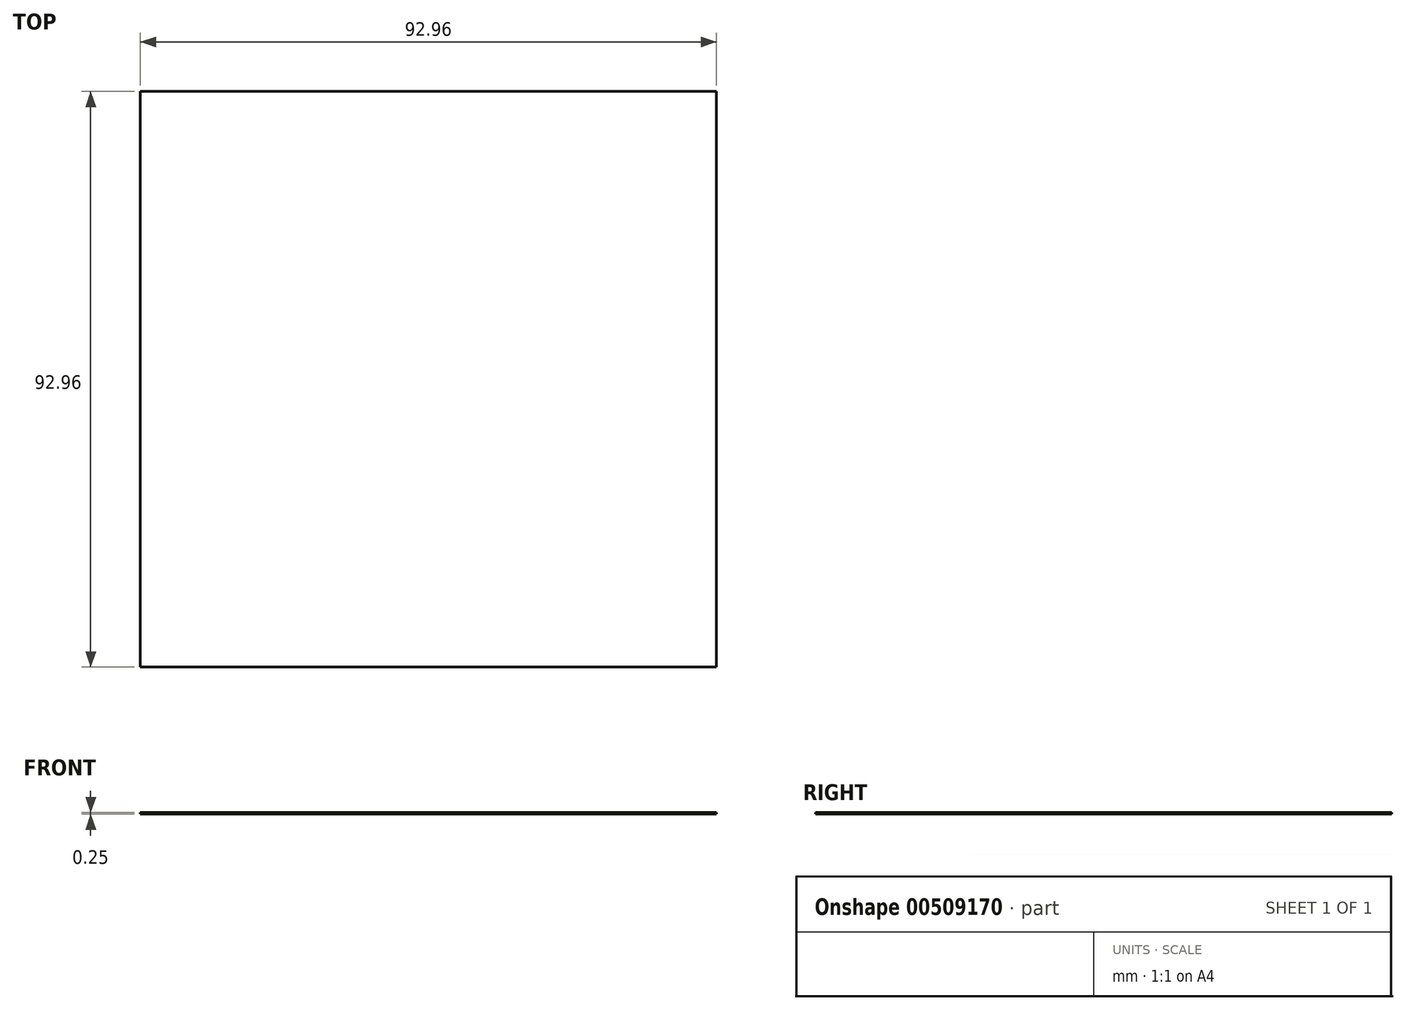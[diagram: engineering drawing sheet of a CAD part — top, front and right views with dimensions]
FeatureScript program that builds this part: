
annotation { "Feature Type Name" : "Feature", "Feature Type Description" : "" }
export const myFeature = defineFeature(function(context is Context, id is Id, definition is map)
    precondition{}
    {
        {
            var Q0;
            Q0=qCreatedBy(makeId("Top.planeOp"),FACE);
            var sketch = newSketch(context, id + "F0", { "sketchPlane" : qUnion([Q0])});
            skLineSegment(sketch, "E0.bottom", {"start": v(-45.47, 44.32) * mm, "end": v(47.49, 44.32) * mm});
            skLineSegment(sketch, "E0.top", {"start": v(-45.47, -48.64) * mm, "end": v(47.49, -48.64) * mm});
            skLineSegment(sketch, "E0.left", {"start": v(-45.47, 44.32) * mm, "end": v(-45.47, -48.64) * mm});
            skLineSegment(sketch, "E0.right", {"start": v(47.49, 44.32) * mm, "end": v(47.49, -48.64) * mm});
            skSolve(sketch);
        }
        {
            var Q0;
            Q0=makeQuery(id+"F0.imprint","IMPRINT",FACE,{"disambiguationData":[TD([[makeQuery(id+"F0.imprint","IMPRINT",EDGE,{"derivedFrom":sQuery(id+"F0.wireOp",EDGE,"E0.bottom")}),-1.0]])]});
            extrude(context, id + "F1", {"entities" : qUnion([Q0]), "depth" : 0.25 * mm});
        }
    });
